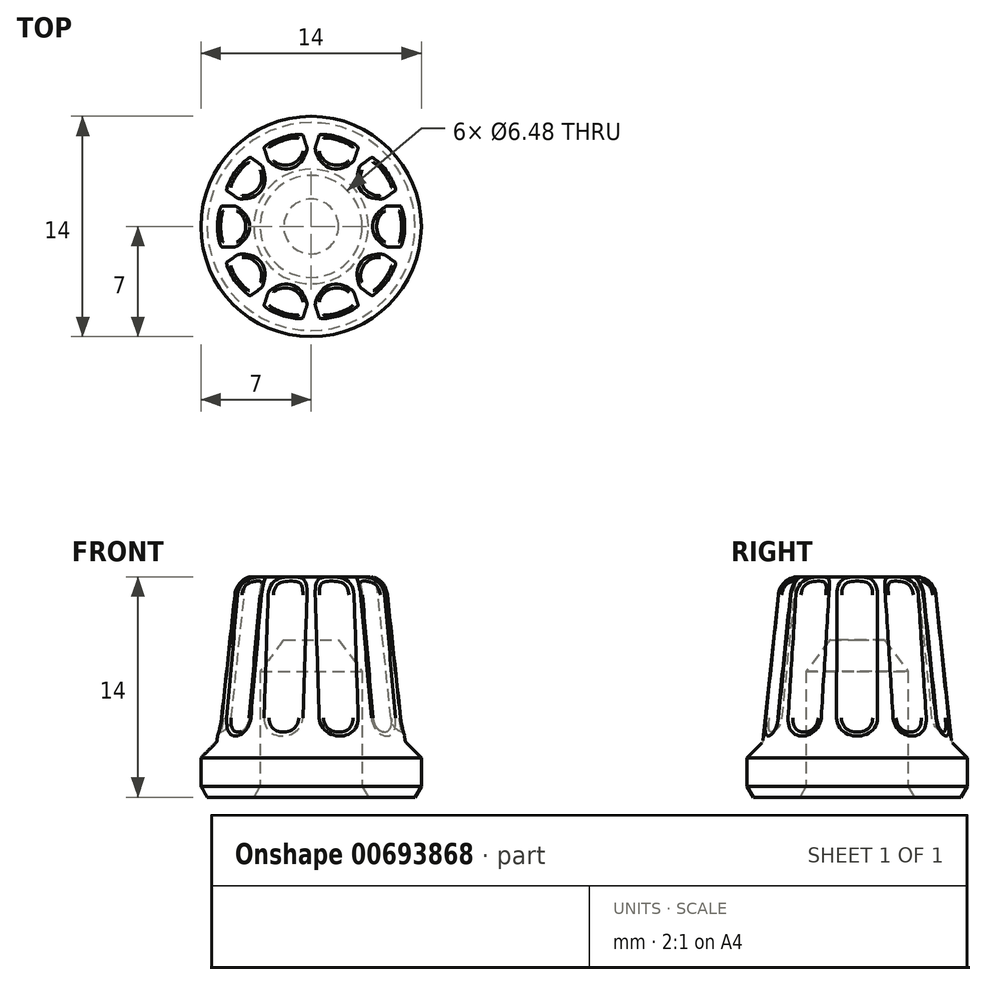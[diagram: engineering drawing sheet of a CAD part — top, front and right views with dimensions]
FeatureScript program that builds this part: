
annotation { "Feature Type Name" : "Feature", "Feature Type Description" : "" }
export const myFeature = defineFeature(function(context is Context, id is Id, definition is map)
    precondition{}
    {
        {
            var Q0;
            Q0=qCreatedBy(makeId("Front.planeOp"),FACE);
            var sketch = newSketch(context, id + "F0", { "sketchPlane" : qUnion([Q0])});
            skLineSegment(sketch, "E0.0", {"start": v(0, 0) * mm, "end": v(7, 0) * mm});
            skLineSegment(sketch, "E1", {"start": v(0, -1.54) * mm, "end": v(0, 15.97) * mm, "construction": true});
            skLineSegment(sketch, "E2", {"start": v(7, 0) * mm, "end": v(7, 2.5) * mm});
            skLineSegment(sketch, "E3", {"start": v(7, 2.5) * mm, "end": v(5.98, 3.52) * mm});
            skLineSegment(sketch, "E4", {"start": v(5.98, 3.52) * mm, "end": v(5, 12.86) * mm});
            skLineSegment(sketch, "E5", {"start": v(3.74, 14) * mm, "end": v(0, 14) * mm});
            skPoint(sketch, "E6.visualSharp", {"position": v(4.88, 14) * mm});
            skArc(sketch, "E6.filletArc", {"start": v(5, 12.86) * mm, "mid": v(4.59, 13.67) * mm, "end": v(3.74, 14) * mm});
            skLineSegment(sketch, "E7", {"start": v(0, 14) * mm, "end": v(0, 0) * mm});
            skLineSegment(sketch, "E8", {"start": v(0, 10) * mm, "end": v(3.24, 10) * mm});
            skLineSegment(sketch, "E9", {"start": v(0, 14) * mm, "end": v(4.83, 14.5) * mm, "construction": true});
            skLineSegment(sketch, "E10", {"start": v(5, 12.86) * mm, "end": v(4.67, 15.97) * mm, "construction": true});
            skPoint(sketch, "E11", {"position": v(4.83, 14.5) * mm});
            skLineSegment(sketch, "E12", {"start": v(3.24, 0) * mm, "end": v(3.24, 10) * mm});
            skSolve(sketch);
        }
        {
            var Q0;
            {var subQ0=sQuery(id+"F0.wireOp",EDGE,"E2");Q0=makeQuery(id+"F0.imprint","IMPRINT",FACE,{"disambiguationData":[TD([[makeQuery(id+"F0.imprint","IMPRINT",EDGE,{"derivedFrom":subQ0}),1.0]])]});}
            var Q1;
            Q1=sQuery(id+"F0.wireOp",EDGE,"E1");
            revolve(context, id + "F1", {"entities" : qUnion([Q0]), "axis" : qUnion([Q1]), "revolveType" : RevolveType.FULL});
        }
        {
            var Q0;
            Q0=sQuery(id+"F0.wireOp",VERTEX,"E11");
            var Q1;
            Q1=sQuery(id+"F0.wireOp",EDGE,"E10");
            cPlane(context, id + "F2", {"entities" : qUnion([Q0, Q1]), "cplaneType" : CPlaneType.LINE_POINT, "offset" : 25.4 * mm, "width" : 152.4 * mm, "height" : 152.4 * mm});
        }
        {
            var Q0;
            Q0=qCreatedBy(id+"F2.planeOp",FACE);
            var sketch = newSketch(context, id + "F3", { "sketchPlane" : qUnion([Q0])});
            skCircle(sketch, "E13", {"center": v(6.82, 0) * mm, "radius": 1.25 * mm});
            skSolve(sketch);
        }
        {
            var Q0;
            Q0=makeQuery(id+"F3.imprint","IMPRINT",FACE,{"disambiguationData":[TD([[makeQuery(id+"F3.imprint","IMPRINT",EDGE,{"derivedFrom":sQuery(id+"F3.wireOp",EDGE,"E13")}),1.0]])]});
            extrude(context, id + "F4", {"entities" : qUnion([Q0]), "oppositeDirection" : true, "depth" : 21 * mm, "offsetDistance" : 25.4 * mm, "symmetric" : true});
        }
        {
            var Q0;
            Q0=makeQuery(id+"F4.opExtrude","CAP_FACE",FACE,{"disambiguationData":[OSD([sQuery(id+"F3.wireOp",EDGE,"E13")])],"isStart":true});
            var Q1;
            Q1=makeQuery(id+"F4.opExtrude","CAP_FACE",FACE,{"disambiguationData":[OSD([sQuery(id+"F3.wireOp",EDGE,"E13")])],"isStart":false});
            fillet(context, id + "F5", {"entities" : qUnion([Q0, Q1]), "radius" : 1 * mm, "allowEdgeOverflow" : false});
        }
        {
            var Q0;
            Q0=makeQuery(id+"F4.opExtrude","SWEPT_BODY",BODY,{"disambiguationData":[OSD([sQuery(id+"F3.wireOp",EDGE,"E13")])]});
            var Q1;
            Q1=sQuery(id+"F0.wireOp",EDGE,"E1");
            circularPattern(context, id + "F6", {"operationType" : NewBodyOperationType.REMOVE, "entities" : qUnion([Q0]), "axis" : qUnion([Q1]), "angle" : 360 * degree, "instanceCount" : 10, "equalSpace" : true});
        }
        {
            var Q0;
            Q0=makeQuery(id+"F1.opRevolve","SWEPT_FACE",FACE,{"disambiguationData":[OSD([sQuery(id+"F0.wireOp",EDGE,"E4")])]});
            fillet(context, id + "F7", {"entities" : qUnion([Q0]), "radius" : .3 * mm, "tangentPropagation" : true, "allowEdgeOverflow" : false});
        }
        {
            var Q0;
            Q0=makeQuery(id+"F1.opRevolve","SWEPT_EDGE",EDGE,{"disambiguationData":[OSD([sQuery(id+"F0.wireOp",EDGE,"E0.0"),sQuery(id+"F0.wireOp",EDGE,"E2")])]});
            var Q1;
            Q1=makeQuery(id+"F1.opRevolve","SWEPT_EDGE",EDGE,{"disambiguationData":[OSD([sQuery(id+"F0.wireOp",EDGE,"E0.0"),sQuery(id+"F0.wireOp",EDGE,"E12")])]});
            chamfer(context, id + "F8", {"entities" : qUnion([Q0, Q1]), "chamferType" : ChamferType.TWO_OFFSETS, "width1" : .4 * mm, "oppositeDirection" : false, "width2" : .7 * mm, "tangentPropagation" : true});
        }
        {
            var Q0;
            Q0=makeQuery(id+"F1.opRevolve","SWEPT_EDGE",EDGE,{"disambiguationData":[OSD([sQuery(id+"F0.wireOp",EDGE,"E8"),sQuery(id+"F0.wireOp",EDGE,"E12")])]});
            chamfer(context, id + "F9", {"entities" : qUnion([Q0]), "chamferType" : ChamferType.TWO_OFFSETS, "width1" : 1.5 * mm, "oppositeDirection" : false, "width2" : 2 * mm, "tangentPropagation" : true});
        }
    });
